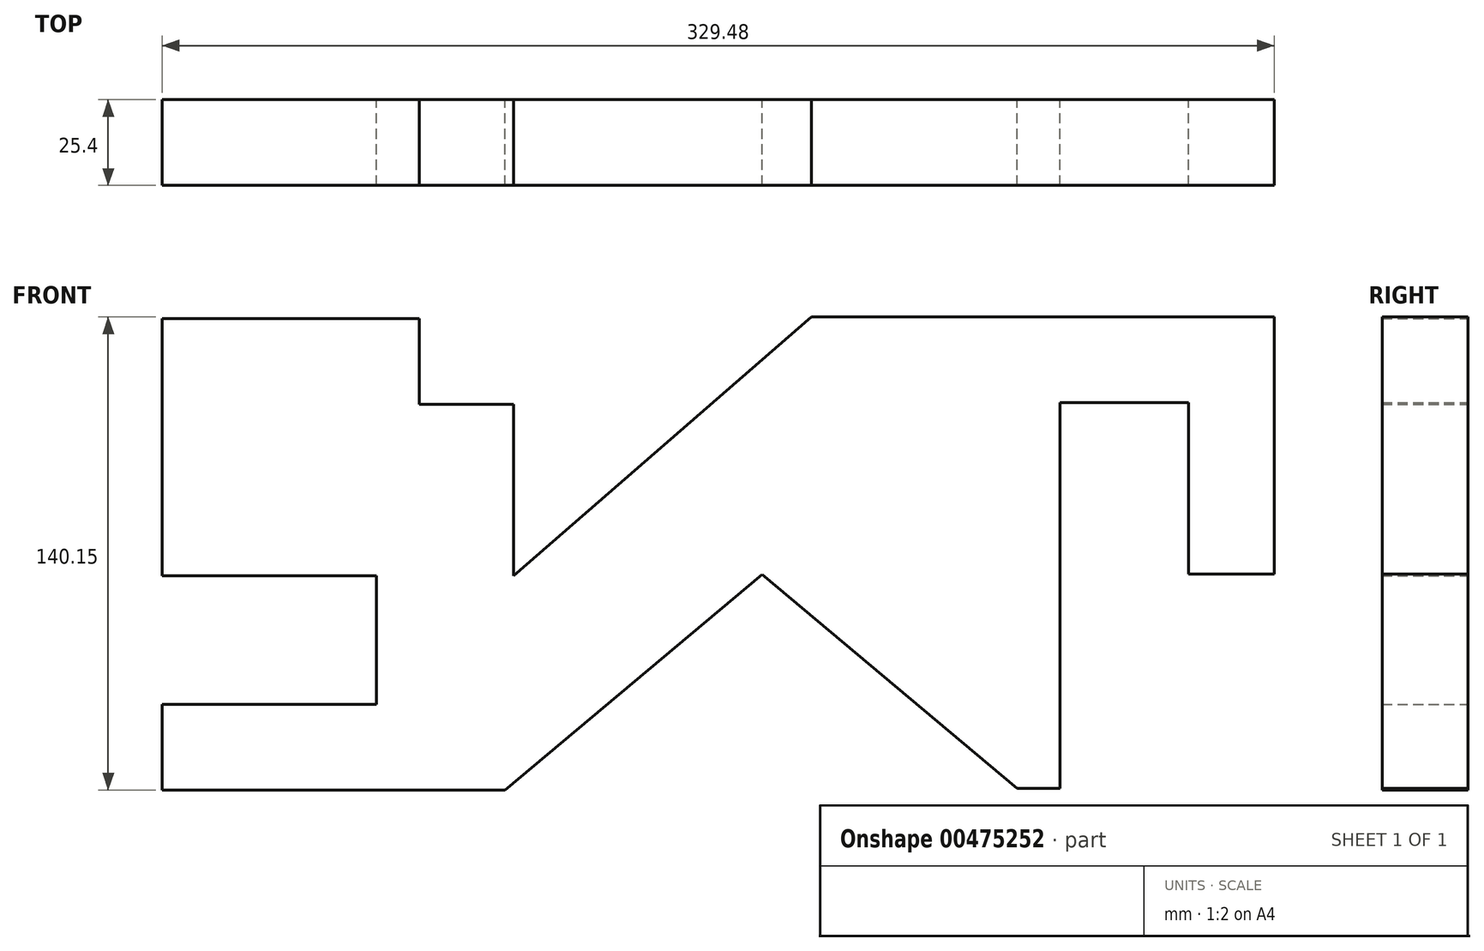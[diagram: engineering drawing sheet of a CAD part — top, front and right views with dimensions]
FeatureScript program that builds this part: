
annotation { "Feature Type Name" : "Feature", "Feature Type Description" : "" }
export const myFeature = defineFeature(function(context is Context, id is Id, definition is map)
    precondition{}
    {
        {
            var Q0;
            Q0=qCreatedBy(makeId("Front.planeOp"),FACE);
            var sketch = newSketch(context, id + "F0", { "sketchPlane" : qUnion([Q0])});
            skLineSegment(sketch, "E0", {"start": v(0, 0) * mm, "end": v(76.2, 0) * mm});
            skLineSegment(sketch, "E1", {"start": v(76.2, 0) * mm, "end": v(76.2, -25.4) * mm});
            skLineSegment(sketch, "E2", {"start": v(76.2, -25.4) * mm, "end": v(104.14, -25.4) * mm});
            skLineSegment(sketch, "E3", {"start": v(104.14, -25.4) * mm, "end": v(104.14, -76.2) * mm});
            skLineSegment(sketch, "E4", {"start": v(104.14, -76.2) * mm, "end": v(192.32, 0.45) * mm});
            skLineSegment(sketch, "E5", {"start": v(192.32, 0.45) * mm, "end": v(329.48, 0.45) * mm});
            skLineSegment(sketch, "E6", {"start": v(329.48, 0.45) * mm, "end": v(329.48, -75.75) * mm});
            skLineSegment(sketch, "E7", {"start": v(329.48, -75.75) * mm, "end": v(304.08, -75.75) * mm});
            skLineSegment(sketch, "E8", {"start": v(304.08, -75.75) * mm, "end": v(304.08, -24.95) * mm});
            skLineSegment(sketch, "E9", {"start": v(304.08, -24.95) * mm, "end": v(265.98, -24.95) * mm});
            skLineSegment(sketch, "E10", {"start": v(265.98, -24.95) * mm, "end": v(265.98, -139.25) * mm});
            skLineSegment(sketch, "E11", {"start": v(265.98, -139.25) * mm, "end": v(253.28, -139.25) * mm});
            skLineSegment(sketch, "E12", {"start": v(0, 0) * mm, "end": v(0, -76.2) * mm});
            skLineSegment(sketch, "E13", {"start": v(0, -76.2) * mm, "end": v(63.5, -76.2) * mm});
            skLineSegment(sketch, "E14", {"start": v(63.5, -76.2) * mm, "end": v(63.5, -114.3) * mm});
            skLineSegment(sketch, "E15", {"start": v(63.5, -114.3) * mm, "end": v(0, -114.3) * mm});
            skLineSegment(sketch, "E16", {"start": v(0, -114.3) * mm, "end": v(0, -139.7) * mm});
            skLineSegment(sketch, "E17", {"start": v(0, -139.7) * mm, "end": v(101.6, -139.7) * mm});
            skLineSegment(sketch, "E18", {"start": v(101.6, -139.7) * mm, "end": v(177.71, -75.84) * mm});
            skLineSegment(sketch, "E19", {"start": v(177.71, -75.84) * mm, "end": v(253.28, -139.25) * mm});
            skSolve(sketch);
        }
        {
            var Q0;
            Q0 = qSketchRegion(id + "F0", true);
            extrude(context, id + "F1", {"entities" : qUnion([Q0]), "depth" : 25.4 * mm});
        }
    });
